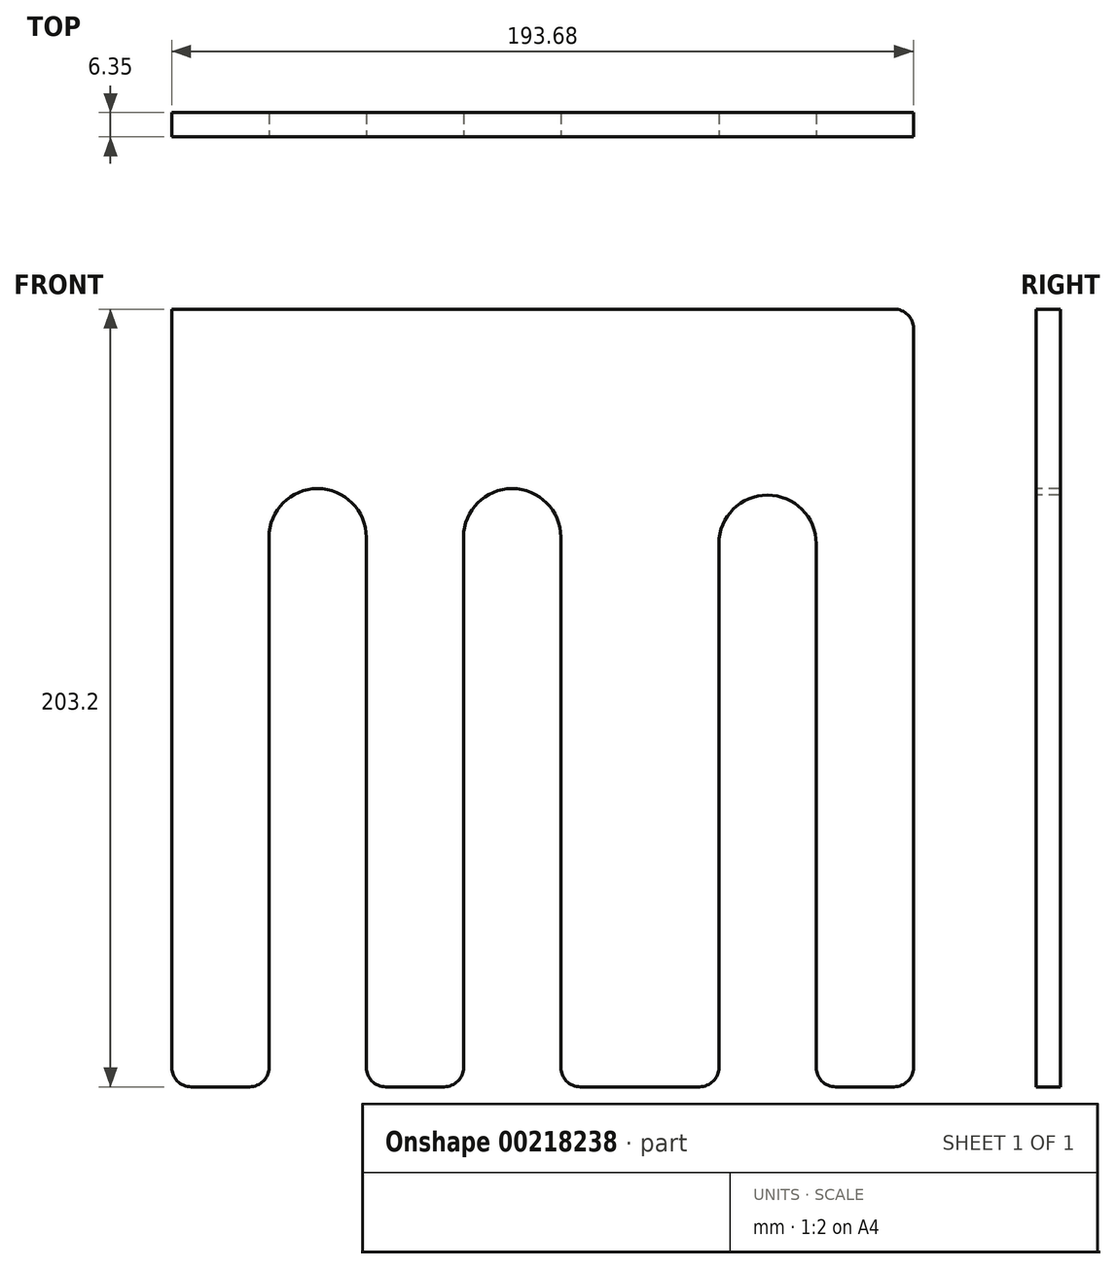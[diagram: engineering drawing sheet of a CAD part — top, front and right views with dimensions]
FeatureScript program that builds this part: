
annotation { "Feature Type Name" : "Feature", "Feature Type Description" : "" }
export const myFeature = defineFeature(function(context is Context, id is Id, definition is map)
    precondition{}
    {
        {
            var Q0;
            Q0=qCreatedBy(makeId("Front.planeOp"),FACE);
            var sketch = newSketch(context, id + "F0", { "sketchPlane" : qUnion([Q0])});
            skLineSegment(sketch, "E0.bottom", {"start": v(-119.44, 112.35) * mm, "end": v(74.24, 112.35) * mm});
            skLineSegment(sketch, "E0.top", {"start": v(-119.44, -90.85) * mm, "end": v(-94.04, -90.85) * mm});
            skLineSegment(sketch, "E0.left", {"start": v(-119.44, 112.35) * mm, "end": v(-119.44, -90.85) * mm});
            skLineSegment(sketch, "E0.right", {"start": v(74.24, 112.35) * mm, "end": v(74.24, -90.85) * mm});
            skLineSegment(sketch, "E1.left", {"start": v(-94.04, 52.76) * mm, "end": v(-94.04, -90.85) * mm});
            skLineSegment(sketch, "E1.right", {"start": v(-68.64, 52.76) * mm, "end": v(-68.64, -90.85) * mm});
            skLineSegment(sketch, "E2.left", {"start": v(-43.24, 52.77) * mm, "end": v(-43.24, -90.85) * mm});
            skLineSegment(sketch, "E2.right", {"start": v(-17.84, 52.77) * mm, "end": v(-17.84, -90.85) * mm});
            skLineSegment(sketch, "E3.left", {"start": v(23.44, 51.07) * mm, "end": v(23.44, -90.85) * mm});
            skLineSegment(sketch, "E3.right", {"start": v(48.84, 51.07) * mm, "end": v(48.84, -90.85) * mm});
            skArc(sketch, "E4", {"start": v(-94.04, 52.76) * mm, "mid": v(-81.34, 65.46) * mm, "end": v(-68.64, 52.76) * mm});
            skArc(sketch, "E5", {"start": v(-43.24, 52.77) * mm, "mid": v(-30.54, 65.47) * mm, "end": v(-17.84, 52.77) * mm});
            skArc(sketch, "E6", {"start": v(23.44, 51.07) * mm, "mid": v(36.14, 63.77) * mm, "end": v(48.84, 51.07) * mm});
            skLineSegment(sketch, "E7", {"start": v(-68.64, -90.85) * mm, "end": v(-43.24, -90.85) * mm});
            skLineSegment(sketch, "E8", {"start": v(48.84, -90.85) * mm, "end": v(74.24, -90.85) * mm});
            skLineSegment(sketch, "E9.trimOffspring", {"start": v(-17.84, -90.85) * mm, "end": v(23.44, -90.85) * mm});
            skSolve(sketch);
        }
        {
            var Q0;
            Q0=makeQuery(id+"F0.imprint","IMPRINT",FACE,{"disambiguationData":[TD([[makeQuery(id+"F0.imprint","IMPRINT",EDGE,{"derivedFrom":sQuery(id+"F0.wireOp",EDGE,"E0.bottom")}),-1.0]])]});
            extrude(context, id + "F1", {"entities" : qUnion([Q0]), "oppositeDirection" : true, "depth" : 6.35 * mm});
        }
        {
            var Q0;
            Q0=makeQuery(id+"F1.opExtrude","SWEPT_EDGE",EDGE,{"disambiguationData":[OSD([sQuery(id+"F0.wireOp",EDGE,"E1.left"),sQuery(id+"F0.wireOp",EDGE,"E0.top")])]});
            var Q1;
            Q1=makeQuery(id+"F1.opExtrude","SWEPT_EDGE",EDGE,{"disambiguationData":[OSD([sQuery(id+"F0.wireOp",EDGE,"E1.right"),sQuery(id+"F0.wireOp",EDGE,"E7")])]});
            var Q2;
            Q2=makeQuery(id+"F1.opExtrude","SWEPT_EDGE",EDGE,{"disambiguationData":[OSD([sQuery(id+"F0.wireOp",EDGE,"E2.left"),sQuery(id+"F0.wireOp",EDGE,"E7")])]});
            var Q3;
            Q3=makeQuery(id+"F1.opExtrude","SWEPT_EDGE",EDGE,{"disambiguationData":[OSD([sQuery(id+"F0.wireOp",EDGE,"E2.right"),sQuery(id+"F0.wireOp",EDGE,"E9.trimOffspring")])]});
            var Q4;
            Q4=makeQuery(id+"F1.opExtrude","SWEPT_EDGE",EDGE,{"disambiguationData":[OSD([sQuery(id+"F0.wireOp",EDGE,"E3.left"),sQuery(id+"F0.wireOp",EDGE,"E9.trimOffspring")])]});
            var Q5;
            Q5=makeQuery(id+"F1.opExtrude","SWEPT_EDGE",EDGE,{"disambiguationData":[OSD([sQuery(id+"F0.wireOp",EDGE,"E3.right"),sQuery(id+"F0.wireOp",EDGE,"E8")])]});
            var Q6;
            Q6=makeQuery(id+"F1.opExtrude","SWEPT_EDGE",EDGE,{"disambiguationData":[OSD([sQuery(id+"F0.wireOp",EDGE,"E0.right"),sQuery(id+"F0.wireOp",EDGE,"E8")])]});
            var Q7;
            Q7=makeQuery(id+"F1.opExtrude","SWEPT_EDGE",EDGE,{"disambiguationData":[OSD([sQuery(id+"F0.wireOp",EDGE,"E0.left"),sQuery(id+"F0.wireOp",EDGE,"E0.top")])]});
            fillet(context, id + "F2", {"entities" : qUnion([Q0, Q1, Q2, Q3, Q4, Q5, Q6, Q7]), "radius" : 5.08 * mm, "tangentPropagation" : true, "allowEdgeOverflow" : false});
        }
    });
